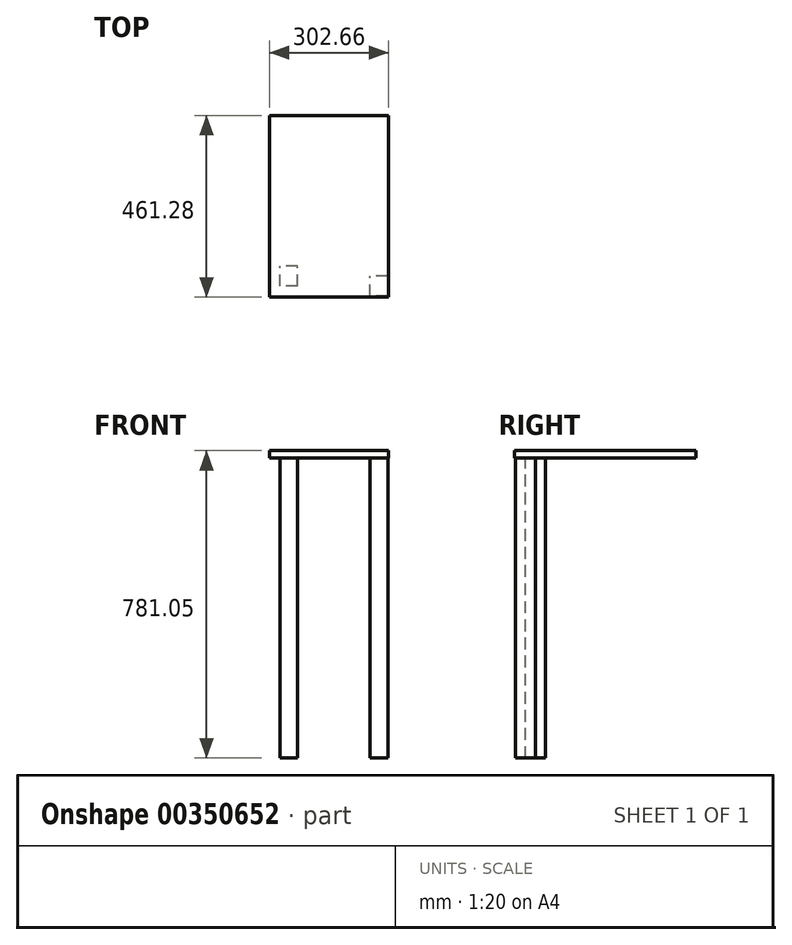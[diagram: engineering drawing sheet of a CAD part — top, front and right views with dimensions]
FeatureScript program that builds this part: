
annotation { "Feature Type Name" : "Feature", "Feature Type Description" : "" }
export const myFeature = defineFeature(function(context is Context, id is Id, definition is map)
    precondition{}
    {
        {
            var Q0;
            Q0=qCreatedBy(makeId("Top.planeOp"),FACE);
            var sketch = newSketch(context, id + "F0", { "sketchPlane" : qUnion([Q0])});
            skLineSegment(sketch, "E0.bottom", {"start": v(253.44, 407.95) * mm, "end": v(-49.22, 407.95) * mm});
            skLineSegment(sketch, "E0.top", {"start": v(253.44, -53.33) * mm, "end": v(-49.22, -53.33) * mm});
            skLineSegment(sketch, "E0.left", {"start": v(253.44, 407.95) * mm, "end": v(253.44, -53.33) * mm});
            skLineSegment(sketch, "E0.right", {"start": v(-49.22, 407.95) * mm, "end": v(-49.22, -53.33) * mm});
            skSolve(sketch);
        }
        {
            var Q0;
            Q0=makeQuery(id+"F0.imprint","IMPRINT",FACE,{"disambiguationData":[TD([[makeQuery(id+"F0.imprint","IMPRINT",EDGE,{"derivedFrom":sQuery(id+"F0.wireOp",EDGE,"E0.bottom")}),1.0]])]});
            extrude(context, id + "F1", {"entities" : qUnion([Q0]), "depth" : 19.05 * mm});
        }
        {
            var Q0;
            Q0=qCreatedBy(makeId("Top.planeOp"),FACE);
            var sketch = newSketch(context, id + "F2", { "sketchPlane" : qUnion([Q0])});
            skLineSegment(sketch, "E1.bottom", {"start": v(252.23, -50.88) * mm, "end": v(206.88, -50.88) * mm});
            skLineSegment(sketch, "E1.top", {"start": v(252.23, 0) * mm, "end": v(206.88, 0) * mm});
            skLineSegment(sketch, "E1.left", {"start": v(252.23, -50.88) * mm, "end": v(252.23, 0) * mm});
            skLineSegment(sketch, "E1.right", {"start": v(206.88, -50.88) * mm, "end": v(206.88, 0) * mm});
            skLineSegment(sketch, "E2.bottom", {"start": v(22.67, -25.44) * mm, "end": v(-22.67, -25.44) * mm});
            skLineSegment(sketch, "E2.top", {"start": v(22.67, 25.44) * mm, "end": v(-22.67, 25.44) * mm});
            skLineSegment(sketch, "E2.left", {"start": v(22.67, -25.44) * mm, "end": v(22.67, 25.44) * mm});
            skLineSegment(sketch, "E2.right", {"start": v(-22.67, -25.44) * mm, "end": v(-22.67, 25.44) * mm});
            skSolve(sketch);
        }
        {
            var Q0;
            Q0=makeQuery(id+"F2.imprint","IMPRINT",FACE,{"disambiguationData":[TD([[makeQuery(id+"F2.imprint","IMPRINT",EDGE,{"derivedFrom":sQuery(id+"F2.wireOp",EDGE,"E1.bottom")}),-1.0]])]});
            var Q1;
            Q1 = qSketchRegion(id + "F2", true);
            extrude(context, id + "F3", {"entities" : qUnion([Q0, Q1]), "operationType" : NewBodyOperationType.ADD, "depth" : -762 * mm});
        }
    });
